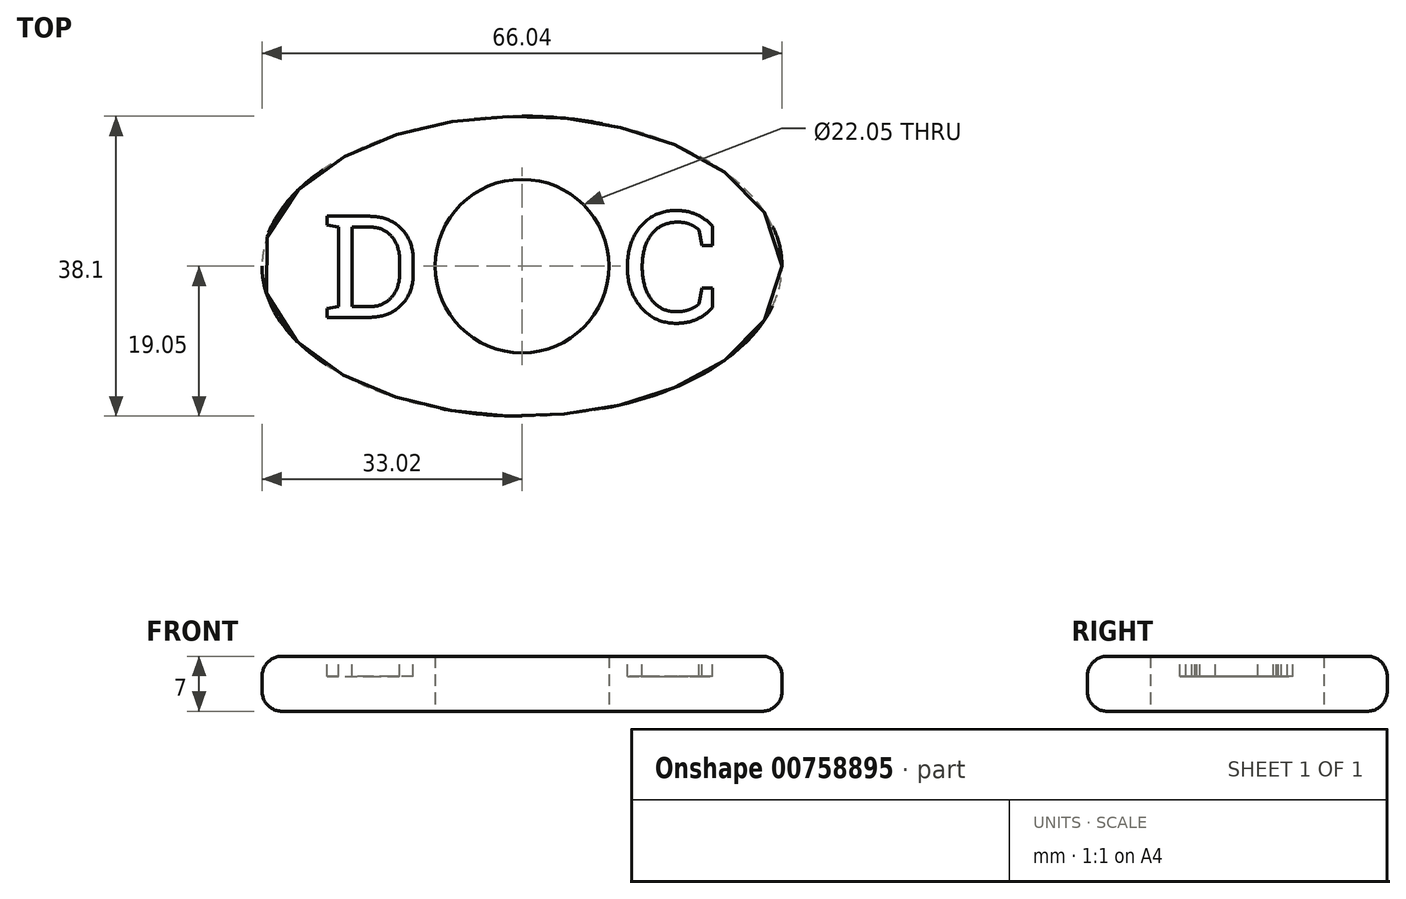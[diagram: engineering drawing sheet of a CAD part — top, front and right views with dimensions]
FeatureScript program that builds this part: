
annotation { "Feature Type Name" : "Feature", "Feature Type Description" : "" }
export const myFeature = defineFeature(function(context is Context, id is Id, definition is map)
    precondition{}
    {
        {
            var Q0;
            Q0=qCreatedBy(makeId("Top.planeOp"),FACE);
            var sketch = newSketch(context, id + "F0", { "sketchPlane" : qUnion([Q0])});
            skEllipse(sketch, "E0", {"center": v(0, 0) * mm, "majorRadius": 33.02 * mm, "minorRadius": 19.05 * mm, "majorAxis": v(1, 0)});
            skCircle(sketch, "E1", {"center": v(0, 0) * mm, "radius": 11.03 * mm});
            skLineSegment(sketch, "E2", {"start": v(-33.02, 0) * mm, "end": v(33.02, 0) * mm, "construction": true});
            skLineSegment(sketch, "E3", {"start": v(0, 19.05) * mm, "end": v(0, -19.05) * mm, "construction": true});
            skSolve(sketch);
        }
        {
            var Q0;
            Q0=makeQuery(id+"F0.imprint","IMPRINT",FACE,{"disambiguationData":[TD([[makeQuery(id+"F0.imprint","IMPRINT",EDGE,{"derivedFrom":sQuery(id+"F0.wireOp",EDGE,"E0")}),1.0]])]});
            extrude(context, id + "F1", {"entities" : qUnion([Q0]), "depth" : 7 * mm, "offsetDistance" : 25.4 * mm});
        }
        {
            var Q0;
            Q0=makeQuery(id+"F1.opExtrude","CAP_EDGE",EDGE,{"disambiguationData":[OSD([sQuery(id+"F0.wireOp",EDGE,"E0")])],"isStart":false});
            var Q1;
            Q1=makeQuery(id+"F1.opExtrude","CAP_EDGE",EDGE,{"disambiguationData":[OSD([sQuery(id+"F0.wireOp",EDGE,"E0")])],"isStart":true});
            fillet(context, id + "F2", {"entities" : qUnion([Q0, Q1]), "radius" : 2.54 * mm, "tangentPropagation" : true, "allowEdgeOverflow" : false});
        }
        {
            var Q0;
            Q0=makeQuery(id+"F1.opExtrude","CAP_FACE",FACE,{"disambiguationData":[OSD([sQuery(id+"F0.wireOp",EDGE,"E0"),sQuery(id+"F0.wireOp",EDGE,"E1")])],"isStart":false});
            var sketch = newSketch(context, id + "F3", { "sketchPlane" : qUnion([Q0])});
            skSolve(sketch);
        }
        {
            var Q0;
            {var subQ0=sQuery(id+"F0.wireOp",EDGE,"E1");Q0=makeQuery(id+"F3.imprint","IMPRINT",FACE,{"disambiguationData":[TD([[makeQuery(id+"F3.imprint","IMPRINT",EDGE,{"derivedFrom":makeQuery(id+"F1.opExtrude","CAP_EDGE",EDGE,{"disambiguationData":[OSD([subQ0])],"isStart":false})}),-1.0]])]});}
            var sketch = newSketch(context, id + "F4", { "sketchPlane" : qUnion([Q0])});
            skText(sketch, "E4", { "text": "D", "fontName": "RobotoSlab-Regular.ttf"});
            skText(sketch, "E5", { "text": "C\n", "fontName": "RobotoSlab-Regular.ttf"});
            skLineSegment(sketch, "E6", {"start": v(0, 0) * mm, "end": v(-25.4, 0) * mm, "construction": true});
            skLineSegment(sketch, "E7", {"start": v(0, 0) * mm, "end": v(25.4, 0) * mm, "construction": true});
            skLineSegment(sketch, "E8", {"start": v(-25.4, 0) * mm, "end": v(-12.7, 0) * mm, "construction": true});
            skLineSegment(sketch, "E9", {"start": v(12.7, 0) * mm, "end": v(25.4, 0) * mm});
            skPoint(sketch, "E10", {"position": v(19.05, 0) * mm});
            skLineSegment(sketch, "E11", {"start": v(12.7, 0) * mm, "end": v(25.4, 0) * mm, "construction": true});
            skPoint(sketch, "E12", {"position": v(-19.05, 0) * mm});
            const initialGuessF4  = {"E4": [-0.0254, -0.0065, 1, 0, 0.013], "E5": [0.0127, -0.00706, 1, 0, 0.01411]};
            skSetInitialGuess(sketch, initialGuessF4);
            skSolve(sketch);
        }
        {
            var Q0;
            Q0=qSketchRegion(id+"F4",true);
            extrude(context, id + "F5", {"entities" : qUnion([Q0]), "operationType" : NewBodyOperationType.REMOVE, "oppositeDirection" : true, "depth" : 2.54 * mm, "offsetDistance" : 25.4 * mm});
        }
    });
